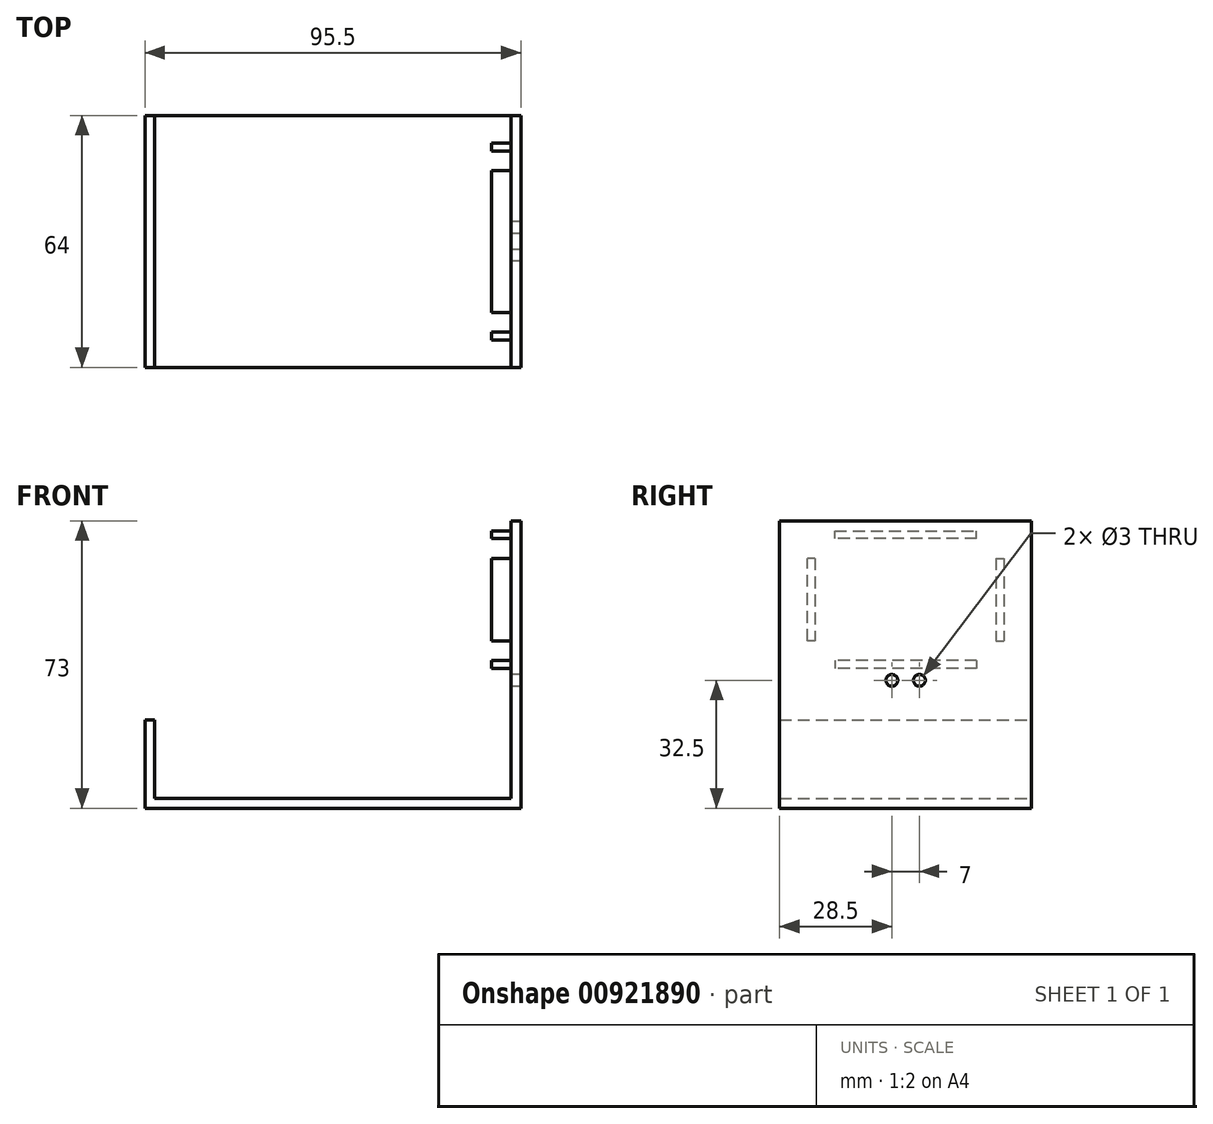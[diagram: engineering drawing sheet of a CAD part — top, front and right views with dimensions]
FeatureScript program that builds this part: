
annotation { "Feature Type Name" : "Feature", "Feature Type Description" : "" }
export const myFeature = defineFeature(function(context is Context, id is Id, definition is map)
    precondition{}
    {
        {
            var Q0;
            Q0=qCreatedBy(makeId("Top.planeOp"),FACE);
            var sketch = newSketch(context, id + "F0", { "sketchPlane" : qUnion([Q0])});
            skLineSegment(sketch, "E0.bottom", {"start": v(0, 0) * mm, "end": v(95.5, 0) * mm});
            skLineSegment(sketch, "E0.top", {"start": v(0, 64) * mm, "end": v(95.5, 64) * mm});
            skLineSegment(sketch, "E0.left", {"start": v(0, 0) * mm, "end": v(0, 64) * mm});
            skLineSegment(sketch, "E0.right", {"start": v(95.5, 0) * mm, "end": v(95.5, 64) * mm});
            skSolve(sketch);
        }
        {
            var Q0;
            Q0=makeQuery(id+"F0.imprint","IMPRINT",FACE,{"disambiguationData":[TD([[makeQuery(id+"F0.imprint","IMPRINT",EDGE,{"derivedFrom":sQuery(id+"F0.wireOp",EDGE,"E0.bottom")}),1.0]])]});
            extrude(context, id + "F1", {"entities" : qUnion([Q0]), "depth" : 2.5 * mm, "offsetDistance" : 25 * mm});
        }
        {
            var Q0;
            Q0=makeQuery(id+"F1.opExtrude","CAP_FACE",FACE,{"disambiguationData":[OSD([sQuery(id+"F0.wireOp",EDGE,"E0.bottom"),sQuery(id+"F0.wireOp",EDGE,"E0.top"),sQuery(id+"F0.wireOp",EDGE,"E0.left"),sQuery(id+"F0.wireOp",EDGE,"E0.right")])],"isStart":false});
            var sketch = newSketch(context, id + "F2", { "sketchPlane" : qUnion([Q0])});
            skLineSegment(sketch, "E1", {"start": v(2.5, 64) * mm, "end": v(2.5, 0) * mm});
            skLineSegment(sketch, "E2", {"start": v(93, 0) * mm, "end": v(93, 64) * mm});
            skSolve(sketch);
        }
        {
            var Q0;
            {var subQ0=sQuery(id+"F2.wireOp",EDGE,"E1");Q0=makeQuery(id+"F2.imprint","IMPRINT",FACE,{"disambiguationData":[TD([[makeQuery(id+"F2.imprint","IMPRINT",EDGE,{"derivedFrom":subQ0}),-1.0]])]});}
            extrude(context, id + "F3", {"entities" : qUnion([Q0]), "operationType" : NewBodyOperationType.ADD, "depth" : 20 * mm, "offsetDistance" : 25 * mm});
        }
        {
            var Q0;
            {var subQ0=sQuery(id+"F2.wireOp",EDGE,"E2");Q0=makeQuery(id+"F2.imprint","IMPRINT",FACE,{"disambiguationData":[TD([[makeQuery(id+"F2.imprint","IMPRINT",EDGE,{"derivedFrom":subQ0}),-1.0]])]});}
            extrude(context, id + "F4", {"entities" : qUnion([Q0]), "operationType" : NewBodyOperationType.ADD, "depth" : 70.5 * mm, "offsetDistance" : 25 * mm});
        }
        {
            var Q0;
            Q0=makeQuery(id+"F4.opExtrude","SWEPT_FACE",FACE,{"disambiguationData":[OSD([sQuery(id+"F2.wireOp",EDGE,"E2")])]});
            var sketch = newSketch(context, id + "F5", { "sketchPlane" : qUnion([Q0])});
            skCircle(sketch, "E3", {"center": v(-35.5, 32.5) * mm, "radius": 1.5 * mm});
            skCircle(sketch, "E4", {"center": v(-28.5, 32.5) * mm, "radius": 1.5 * mm});
            skLineSegment(sketch, "E5.bottom", {"start": v(-55, 68.5) * mm, "end": v(-9, 68.5) * mm});
            skLineSegment(sketch, "E5.top", {"start": v(-55, 37.5) * mm, "end": v(-9, 37.5) * mm});
            skLineSegment(sketch, "E5.left", {"start": v(-55, 68.5) * mm, "end": v(-55, 37.5) * mm});
            skLineSegment(sketch, "E5.right", {"start": v(-9, 68.5) * mm, "end": v(-9, 37.5) * mm});
            skLineSegment(sketch, "E6.bottom", {"start": v(-9, 42.5) * mm, "end": v(-7, 42.5) * mm});
            skLineSegment(sketch, "E6.top", {"start": v(-9, 63.5) * mm, "end": v(-7, 63.5) * mm});
            skLineSegment(sketch, "E6.left", {"start": v(-9, 42.5) * mm, "end": v(-9, 63.5) * mm});
            skLineSegment(sketch, "E6.right", {"start": v(-7, 42.5) * mm, "end": v(-7, 63.5) * mm});
            skLineSegment(sketch, "E7.bottom", {"start": v(-14, 68.5) * mm, "end": v(-50, 68.5) * mm});
            skLineSegment(sketch, "E7.top", {"start": v(-14, 70.5) * mm, "end": v(-50, 70.5) * mm});
            skLineSegment(sketch, "E7.left", {"start": v(-14, 68.5) * mm, "end": v(-14, 70.5) * mm});
            skLineSegment(sketch, "E7.right", {"start": v(-50, 68.5) * mm, "end": v(-50, 70.5) * mm});
            skLineSegment(sketch, "E8.bottom", {"start": v(-55, 63.5) * mm, "end": v(-57, 63.5) * mm});
            skLineSegment(sketch, "E8.top", {"start": v(-55, 42.5) * mm, "end": v(-57, 42.5) * mm});
            skLineSegment(sketch, "E8.left", {"start": v(-55, 63.5) * mm, "end": v(-55, 42.5) * mm});
            skLineSegment(sketch, "E8.right", {"start": v(-57, 63.5) * mm, "end": v(-57, 42.5) * mm});
            skLineSegment(sketch, "E9.bottom", {"start": v(-50, 37.5) * mm, "end": v(-14, 37.5) * mm});
            skLineSegment(sketch, "E9.top", {"start": v(-50, 35.5) * mm, "end": v(-14, 35.5) * mm});
            skLineSegment(sketch, "E9.left", {"start": v(-50, 37.5) * mm, "end": v(-50, 35.5) * mm});
            skLineSegment(sketch, "E9.right", {"start": v(-14, 37.5) * mm, "end": v(-14, 35.5) * mm});
            skSolve(sketch);
        }
        {
            var Q0;
            Q0=makeQuery(id+"F5.imprint","IMPRINT",FACE,{"disambiguationData":[TD([[makeQuery(id+"F5.imprint","IMPRINT",EDGE,{"derivedFrom":sQuery(id+"F5.wireOp",EDGE,"E7.top")}),1.0]])]});
            var Q1;
            {var subQ2=sQuery(id+"F5.wireOp",EDGE,"E6.bottom");Q1=makeQuery(id+"F5.imprint","IMPRINT",FACE,{"disambiguationData":[TD([[makeQuery(id+"F5.imprint","IMPRINT",EDGE,{"derivedFrom":subQ2}),1.0]])]});}
            var Q2;
            Q2=makeQuery(id+"F5.imprint","IMPRINT",FACE,{"disambiguationData":[TD([[makeQuery(id+"F5.imprint","IMPRINT",EDGE,{"derivedFrom":sQuery(id+"F5.wireOp",EDGE,"E9.top")}),1.0]])]});
            var Q3;
            {var subQ0=sQuery(id+"F5.wireOp",EDGE,"E8.bottom");Q3=makeQuery(id+"F5.imprint","IMPRINT",FACE,{"disambiguationData":[TD([[makeQuery(id+"F5.imprint","IMPRINT",EDGE,{"derivedFrom":subQ0}),1.0]])]});}
            extrude(context, id + "F6", {"entities" : qUnion([Q0, Q1, Q2, Q3]), "operationType" : NewBodyOperationType.ADD, "depth" : 5 * mm, "offsetDistance" : 25 * mm});
        }
        {
            var Q0;
            Q0=makeQuery(id+"F5.imprint","IMPRINT",FACE,{"disambiguationData":[TD([[makeQuery(id+"F5.imprint","IMPRINT",EDGE,{"derivedFrom":sQuery(id+"F5.wireOp",EDGE,"E3")}),1.0]])]});
            var Q1;
            Q1=makeQuery(id+"F5.imprint","IMPRINT",FACE,{"disambiguationData":[TD([[makeQuery(id+"F5.imprint","IMPRINT",EDGE,{"derivedFrom":sQuery(id+"F5.wireOp",EDGE,"E4")}),1.0]])]});
            extrude(context, id + "F7", {"entities" : qUnion([Q0, Q1]), "operationType" : NewBodyOperationType.REMOVE, "oppositeDirection" : true, "depth" : 25 * mm, "offsetDistance" : 25 * mm});
        }
    });
